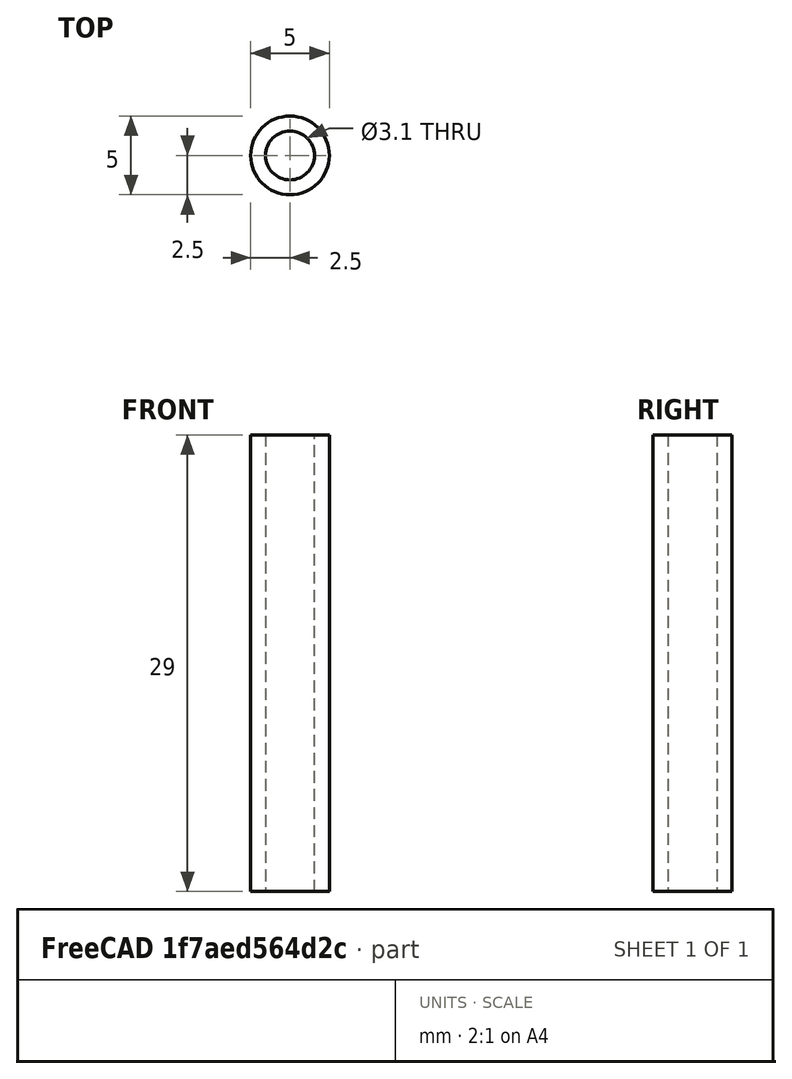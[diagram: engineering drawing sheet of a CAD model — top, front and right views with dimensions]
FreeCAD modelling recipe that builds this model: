
FCSTD DOCUMENT  (FreeCAD 0.20R29410 (Git))
Label: front_pillar
License: All rights reserved
LicenseURL: http://en.wikipedia.org/wiki/All_rights_reserved
objects: PartDesign::CoordinateSystem×2, Sketcher::SketchObject×1, PartDesign::Pad×1, PartDesign::Body×1
note: 6 computed .brp shape members not serialized (recipe doc carries the construction recipe); baked Part::Feature solids carry a one-line shape summary decoded from their .brp

FEATURE [Sketcher::SketchObject] Sketch
  FullyConstrained = true
  MapMode = 5
  Support = -> [XY_Plane]
  sketch-geometry (2):
    g0: Circle CenterX=0 CenterY=0 CenterZ=0 NormalX=0 NormalY=0 NormalZ=1 AngleXU=0 Radius=2.5
    g1: Circle CenterX=0 CenterY=0 CenterZ=0 NormalX=0 NormalY=0 NormalZ=1 AngleXU=0 Radius=1.55
  constraints (4):
    c: Coincident(g0,g-1)
    c: Coincident(g1,g0)
    c: Diameter(g1) = 3.1
    c: Diameter(g0) = 5
FEATURE [PartDesign::Pad] Pad
  Direction = (0,0,1)
  Length = 29
  Length2 = 10
  Profile = -> Sketch
  ReferenceAxis = -> Sketch [N_Axis]
  Type = 0
FEATURE [PartDesign::CoordinateSystem] LCS_1
  AttacherType = Attacher::AttachEngine3D
  MapMode = 11
  Placement = pos=(0,0,0) rot=(0,0,1;1.5708rad)
  Support = -> [Pad]
FEATURE [PartDesign::CoordinateSystem] LCS_2
  AttacherType = Attacher::AttachEngine3D
  MapMode = 11
  Placement = pos=(0,0,29) rot=(0,0,1;1.5708rad)
  Support = -> [Pad]
FEATURE [PartDesign::Body] Body
  Group = -> [Sketch,Pad,LCS_1,LCS_2]
  Origin = -> Origin
  Tip = -> Pad
